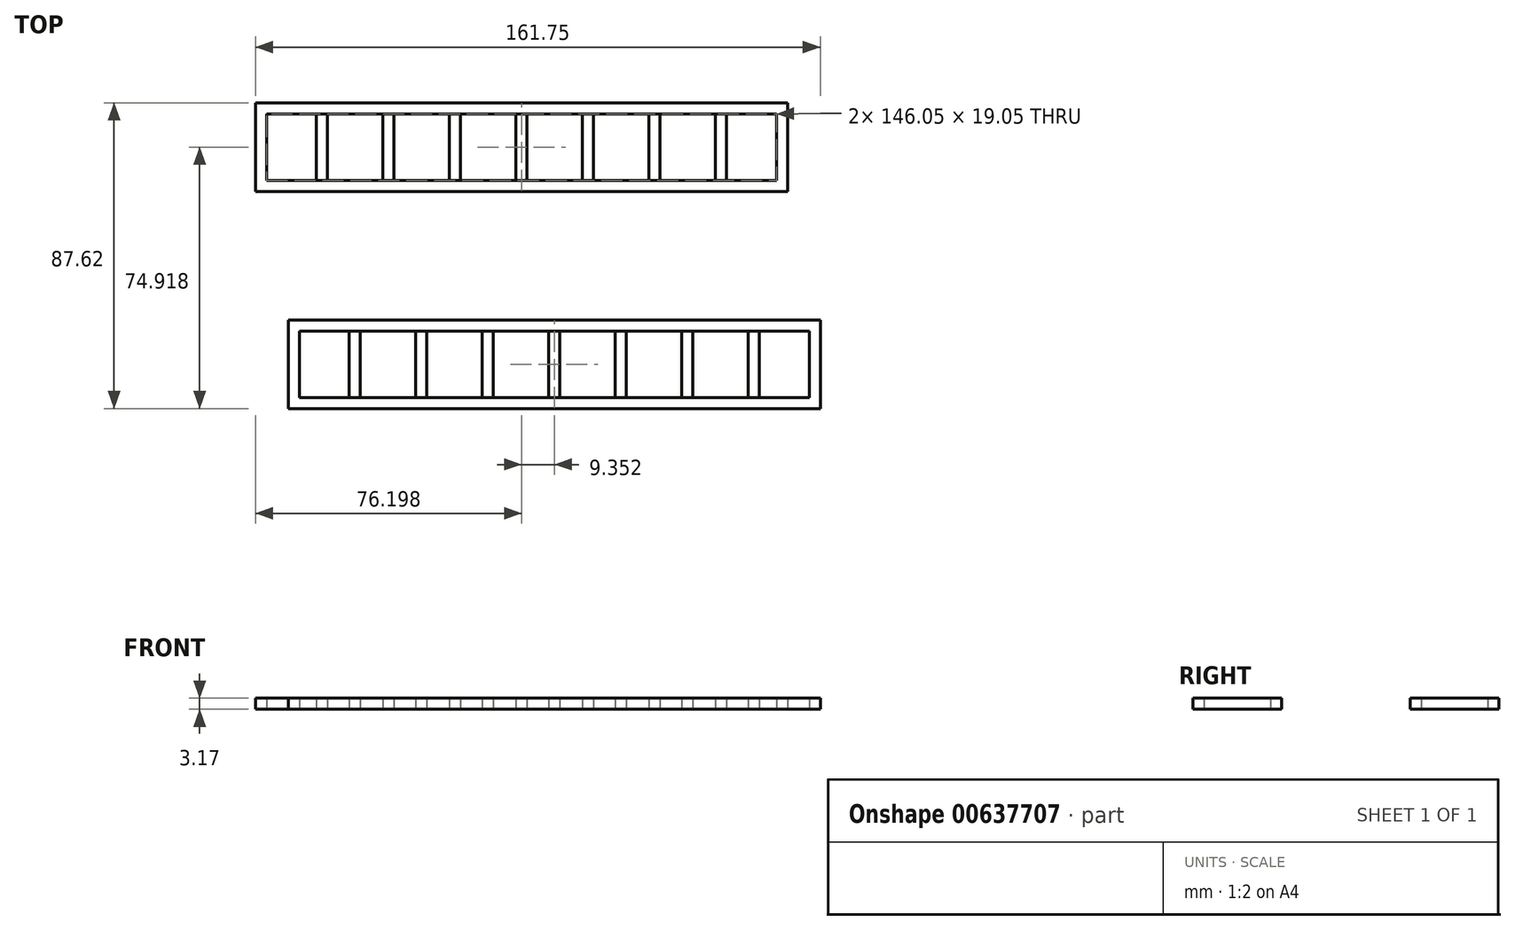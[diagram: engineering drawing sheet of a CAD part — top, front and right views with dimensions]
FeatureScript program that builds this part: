
annotation { "Feature Type Name" : "Feature", "Feature Type Description" : "" }
export const myFeature = defineFeature(function(context is Context, id is Id, definition is map)
    precondition{}
    {
        {
            var Q0;
            Q0=qCreatedBy(makeId("Top.planeOp"),FACE);
            var sketch = newSketch(context, id + "F0", { "sketchPlane" : qUnion([Q0])});
            skLineSegment(sketch, "E0.bottom", {"start": v(-74.02, 8.21) * mm, "end": v(78.38, 8.21) * mm});
            skLineSegment(sketch, "E0.top", {"start": v(-74.02, -17.19) * mm, "end": v(78.38, -17.19) * mm});
            skLineSegment(sketch, "E0.left", {"start": v(-74.02, 8.21) * mm, "end": v(-74.02, -17.19) * mm});
            skLineSegment(sketch, "E0.right", {"start": v(78.38, 8.21) * mm, "end": v(78.38, -17.19) * mm});
            skLineSegment(sketch, "E1.bottom", {"start": v(-83.37, 70.43) * mm, "end": v(69.03, 70.43) * mm});
            skLineSegment(sketch, "E1.top", {"start": v(-83.37, 45.03) * mm, "end": v(69.03, 45.03) * mm});
            skLineSegment(sketch, "E1.left", {"start": v(-83.37, 70.43) * mm, "end": v(-83.37, 45.03) * mm});
            skLineSegment(sketch, "E1.right", {"start": v(69.03, 70.43) * mm, "end": v(69.03, 45.03) * mm});
            skLineSegment(sketch, "E2", {"start": v(-80.2, 70.43) * mm, "end": v(-80.2, 45.03) * mm});
            skLineSegment(sketch, "E3", {"start": v(-83.37, 67.25) * mm, "end": v(69.03, 67.25) * mm});
            skLineSegment(sketch, "E4", {"start": v(65.85, 45.03) * mm, "end": v(65.85, 70.43) * mm});
            skLineSegment(sketch, "E5", {"start": v(69.03, 48.2) * mm, "end": v(-83.37, 48.2) * mm});
            skLineSegment(sketch, "E6", {"start": v(-70.84, 8.21) * mm, "end": v(-70.84, -17.19) * mm});
            skLineSegment(sketch, "E7", {"start": v(-74.02, 5.04) * mm, "end": v(78.38, 5.04) * mm});
            skLineSegment(sketch, "E8", {"start": v(75.2, 8.21) * mm, "end": v(75.2, -17.19) * mm});
            skLineSegment(sketch, "E9", {"start": v(-74.02, -14.01) * mm, "end": v(78.38, -14.01) * mm});
            skLineSegment(sketch, "E10", {"start": v(-54.97, 8.21) * mm, "end": v(-54.97, -17.19) * mm});
            skLineSegment(sketch, "E11", {"start": v(-35.92, 8.21) * mm, "end": v(-35.92, -17.19) * mm});
            skLineSegment(sketch, "E12", {"start": v(-16.87, 8.21) * mm, "end": v(-16.87, -17.19) * mm});
            skLineSegment(sketch, "E13", {"start": v(21.23, 8.21) * mm, "end": v(21.23, -17.19) * mm});
            skLineSegment(sketch, "E14", {"start": v(40.28, 8.21) * mm, "end": v(40.28, -17.19) * mm});
            skLineSegment(sketch, "E15", {"start": v(2.18, 8.21) * mm, "end": v(2.18, -17.19) * mm});
            skLineSegment(sketch, "E16", {"start": v(59.33, 8.21) * mm, "end": v(59.33, -17.19) * mm});
            skLineSegment(sketch, "E17", {"start": v(-64.32, 70.43) * mm, "end": v(-64.32, 45.03) * mm});
            skLineSegment(sketch, "E18", {"start": v(-45.27, 70.43) * mm, "end": v(-45.27, 45.03) * mm});
            skLineSegment(sketch, "E19", {"start": v(-26.22, 70.43) * mm, "end": v(-26.22, 45.03) * mm});
            skLineSegment(sketch, "E20", {"start": v(30.93, 70.43) * mm, "end": v(30.93, 45.03) * mm});
            skLineSegment(sketch, "E21", {"start": v(49.98, 70.43) * mm, "end": v(49.98, 45.03) * mm});
            skLineSegment(sketch, "E22", {"start": v(-7.17, 70.43) * mm, "end": v(-7.17, 45.03) * mm});
            skLineSegment(sketch, "E23", {"start": v(11.88, 70.43) * mm, "end": v(11.88, 45.03) * mm});
            skLineSegment(sketch, "E24", {"start": v(-65.9, 70.43) * mm, "end": v(-65.9, 45.03) * mm});
            skLineSegment(sketch, "E25", {"start": v(-62.73, 70.43) * mm, "end": v(-62.73, 45.03) * mm});
            skLineSegment(sketch, "E26", {"start": v(-46.86, 70.43) * mm, "end": v(-46.86, 45.03) * mm});
            skLineSegment(sketch, "E27", {"start": v(-43.68, 70.43) * mm, "end": v(-43.68, 45.03) * mm});
            skLineSegment(sketch, "E28", {"start": v(-27.8, 70.43) * mm, "end": v(-27.8, 45.03) * mm});
            skLineSegment(sketch, "E29", {"start": v(-24.63, 70.43) * mm, "end": v(-24.63, 45.03) * mm});
            skLineSegment(sketch, "E30", {"start": v(-8.76, 70.43) * mm, "end": v(-8.76, 45.03) * mm});
            skLineSegment(sketch, "E31", {"start": v(-5.58, 70.43) * mm, "end": v(-5.58, 45.03) * mm});
            skLineSegment(sketch, "E32", {"start": v(10.3, 70.43) * mm, "end": v(10.3, 45.03) * mm});
            skLineSegment(sketch, "E33", {"start": v(13.47, 70.43) * mm, "end": v(13.47, 45.03) * mm});
            skLineSegment(sketch, "E34", {"start": v(29.34, 70.43) * mm, "end": v(29.34, 45.03) * mm});
            skLineSegment(sketch, "E35", {"start": v(32.52, 70.43) * mm, "end": v(32.52, 45.03) * mm});
            skLineSegment(sketch, "E36", {"start": v(48.4, 70.43) * mm, "end": v(48.4, 45.03) * mm});
            skLineSegment(sketch, "E37", {"start": v(51.57, 70.43) * mm, "end": v(51.57, 45.03) * mm});
            skLineSegment(sketch, "E38", {"start": v(-56.56, 8.21) * mm, "end": v(-56.56, -17.19) * mm});
            skLineSegment(sketch, "E39", {"start": v(-53.38, 8.21) * mm, "end": v(-53.38, -17.19) * mm});
            skLineSegment(sketch, "E40", {"start": v(-37.5, 8.21) * mm, "end": v(-37.5, -17.19) * mm});
            skLineSegment(sketch, "E41", {"start": v(-34.33, 8.21) * mm, "end": v(-34.33, -17.19) * mm});
            skLineSegment(sketch, "E42", {"start": v(-18.46, 8.21) * mm, "end": v(-18.46, -17.19) * mm});
            skLineSegment(sketch, "E43", {"start": v(-15.28, 8.21) * mm, "end": v(-15.28, -17.19) * mm});
            skLineSegment(sketch, "E44", {"start": v(0.6, 8.21) * mm, "end": v(0.6, -17.19) * mm});
            skLineSegment(sketch, "E45", {"start": v(3.77, 8.21) * mm, "end": v(3.77, -17.19) * mm});
            skLineSegment(sketch, "E46", {"start": v(19.64, 8.21) * mm, "end": v(19.64, -17.19) * mm});
            skLineSegment(sketch, "E47", {"start": v(22.82, 8.21) * mm, "end": v(22.82, -17.19) * mm});
            skLineSegment(sketch, "E48", {"start": v(38.7, 8.21) * mm, "end": v(38.7, -17.19) * mm});
            skLineSegment(sketch, "E49", {"start": v(41.87, 8.21) * mm, "end": v(41.87, -17.19) * mm});
            skLineSegment(sketch, "E50", {"start": v(57.74, 8.21) * mm, "end": v(57.74, -17.19) * mm});
            skLineSegment(sketch, "E51", {"start": v(60.92, 8.21) * mm, "end": v(60.92, -17.19) * mm});
            skSolve(sketch);
        }
        {
            var Q0;
            {var subQ0=sQuery(id+"F0.wireOp",EDGE,"E0.left");var subQ1=sQuery(id+"F0.wireOp",EDGE,"E0.bottom");var subQ2=makeQuery(id+"F0.imprint","INTERSECT",VERTEX,{"derivedFrom":[subQ1,subQ0]});Q0=makeQuery(id+"F0.imprint","IMPRINT",FACE,{"disambiguationData":[TD([[makeQuery(id+"F0.imprint","IMPRINT",EDGE,{"disambiguationData":[TD([[subQ2,-1.0]])],"derivedFrom":subQ1}),-1.0]])]});}
            var Q1;
            {var subQ0=sQuery(id+"F0.wireOp",EDGE,"E0.right");var subQ1=sQuery(id+"F0.wireOp",EDGE,"E0.bottom");var subQ2=makeQuery(id+"F0.imprint","INTERSECT",VERTEX,{"derivedFrom":[subQ1,subQ0]});Q1=makeQuery(id+"F0.imprint","IMPRINT",FACE,{"disambiguationData":[TD([[makeQuery(id+"F0.imprint","IMPRINT",EDGE,{"disambiguationData":[TD([[subQ2,1.0]])],"derivedFrom":subQ1}),-1.0]])]});}
            var Q2;
            {var subQ0=sQuery(id+"F0.wireOp",EDGE,"E0.left");var subQ1=sQuery(id+"F0.wireOp",EDGE,"E0.top");var subQ2=makeQuery(id+"F0.imprint","INTERSECT",VERTEX,{"derivedFrom":[subQ1,subQ0]});Q2=makeQuery(id+"F0.imprint","IMPRINT",FACE,{"disambiguationData":[TD([[makeQuery(id+"F0.imprint","IMPRINT",EDGE,{"disambiguationData":[TD([[subQ2,-1.0]])],"derivedFrom":subQ1}),1.0]])]});}
            var Q3;
            {var subQ0=sQuery(id+"F0.wireOp",EDGE,"E0.right");var subQ1=sQuery(id+"F0.wireOp",EDGE,"E0.top");var subQ2=makeQuery(id+"F0.imprint","INTERSECT",VERTEX,{"derivedFrom":[subQ1,subQ0]});Q3=makeQuery(id+"F0.imprint","IMPRINT",FACE,{"disambiguationData":[TD([[makeQuery(id+"F0.imprint","IMPRINT",EDGE,{"disambiguationData":[TD([[subQ2,1.0]])],"derivedFrom":subQ1}),1.0]])]});}
            var Q4;
            {var subQ0=sQuery(id+"F0.wireOp",EDGE,"E1.right");var subQ1=sQuery(id+"F0.wireOp",EDGE,"E1.bottom");var subQ2=makeQuery(id+"F0.imprint","INTERSECT",VERTEX,{"derivedFrom":[subQ1,subQ0]});Q4=makeQuery(id+"F0.imprint","IMPRINT",FACE,{"disambiguationData":[TD([[makeQuery(id+"F0.imprint","IMPRINT",EDGE,{"disambiguationData":[TD([[subQ2,1.0]])],"derivedFrom":subQ1}),-1.0]])]});}
            var Q5;
            {var subQ0=sQuery(id+"F0.wireOp",EDGE,"E1.left");var subQ1=sQuery(id+"F0.wireOp",EDGE,"E1.top");var subQ2=makeQuery(id+"F0.imprint","INTERSECT",VERTEX,{"derivedFrom":[subQ1,subQ0]});Q5=makeQuery(id+"F0.imprint","IMPRINT",FACE,{"disambiguationData":[TD([[makeQuery(id+"F0.imprint","IMPRINT",EDGE,{"disambiguationData":[TD([[subQ2,-1.0]])],"derivedFrom":subQ1}),1.0]])]});}
            var Q6;
            {var subQ0=sQuery(id+"F0.wireOp",EDGE,"E1.right");var subQ1=sQuery(id+"F0.wireOp",EDGE,"E1.top");var subQ2=makeQuery(id+"F0.imprint","INTERSECT",VERTEX,{"derivedFrom":[subQ1,subQ0]});Q6=makeQuery(id+"F0.imprint","IMPRINT",FACE,{"disambiguationData":[TD([[makeQuery(id+"F0.imprint","IMPRINT",EDGE,{"disambiguationData":[TD([[subQ2,1.0]])],"derivedFrom":subQ1}),1.0]])]});}
            var Q7;
            {var subQ0=sQuery(id+"F0.wireOp",EDGE,"E6");var subQ1=sQuery(id+"F0.wireOp",EDGE,"E0.bottom");var subQ2=makeQuery(id+"F0.imprint","INTERSECT",VERTEX,{"derivedFrom":[subQ1,subQ0]});Q7=makeQuery(id+"F0.imprint","IMPRINT",FACE,{"disambiguationData":[TD([[makeQuery(id+"F0.imprint","IMPRINT",EDGE,{"disambiguationData":[TD([[subQ2,-1.0]])],"derivedFrom":subQ1}),-1.0]])]});}
            var Q8;
            {var subQ0=sQuery(id+"F0.wireOp",EDGE,"E10");var subQ1=sQuery(id+"F0.wireOp",EDGE,"E0.bottom");var subQ2=makeQuery(id+"F0.imprint","INTERSECT",VERTEX,{"derivedFrom":[subQ1,subQ0]});Q8=makeQuery(id+"F0.imprint","IMPRINT",FACE,{"disambiguationData":[TD([[makeQuery(id+"F0.imprint","IMPRINT",EDGE,{"disambiguationData":[TD([[subQ2,1.0]])],"derivedFrom":subQ1}),-1.0]])]});}
            var Q9;
            {var subQ0=sQuery(id+"F0.wireOp",EDGE,"E10");var subQ1=sQuery(id+"F0.wireOp",EDGE,"E0.bottom");var subQ2=makeQuery(id+"F0.imprint","INTERSECT",VERTEX,{"derivedFrom":[subQ1,subQ0]});Q9=makeQuery(id+"F0.imprint","IMPRINT",FACE,{"disambiguationData":[TD([[makeQuery(id+"F0.imprint","IMPRINT",EDGE,{"disambiguationData":[TD([[subQ2,-1.0]])],"derivedFrom":subQ1}),-1.0]])]});}
            var Q10;
            {var subQ0=sQuery(id+"F0.wireOp",EDGE,"E39");var subQ1=sQuery(id+"F0.wireOp",EDGE,"E0.bottom");var subQ2=makeQuery(id+"F0.imprint","INTERSECT",VERTEX,{"derivedFrom":[subQ1,subQ0]});Q10=makeQuery(id+"F0.imprint","IMPRINT",FACE,{"disambiguationData":[TD([[makeQuery(id+"F0.imprint","IMPRINT",EDGE,{"disambiguationData":[TD([[subQ2,-1.0]])],"derivedFrom":subQ1}),-1.0]])]});}
            var Q11;
            {var subQ0=sQuery(id+"F0.wireOp",EDGE,"E11");var subQ1=sQuery(id+"F0.wireOp",EDGE,"E0.bottom");var subQ2=makeQuery(id+"F0.imprint","INTERSECT",VERTEX,{"derivedFrom":[subQ1,subQ0]});Q11=makeQuery(id+"F0.imprint","IMPRINT",FACE,{"disambiguationData":[TD([[makeQuery(id+"F0.imprint","IMPRINT",EDGE,{"disambiguationData":[TD([[subQ2,1.0]])],"derivedFrom":subQ1}),-1.0]])]});}
            var Q12;
            {var subQ0=sQuery(id+"F0.wireOp",EDGE,"E11");var subQ1=sQuery(id+"F0.wireOp",EDGE,"E0.bottom");var subQ2=makeQuery(id+"F0.imprint","INTERSECT",VERTEX,{"derivedFrom":[subQ1,subQ0]});Q12=makeQuery(id+"F0.imprint","IMPRINT",FACE,{"disambiguationData":[TD([[makeQuery(id+"F0.imprint","IMPRINT",EDGE,{"disambiguationData":[TD([[subQ2,-1.0]])],"derivedFrom":subQ1}),-1.0]])]});}
            var Q13;
            {var subQ0=sQuery(id+"F0.wireOp",EDGE,"E41");var subQ1=sQuery(id+"F0.wireOp",EDGE,"E0.bottom");var subQ2=makeQuery(id+"F0.imprint","INTERSECT",VERTEX,{"derivedFrom":[subQ1,subQ0]});Q13=makeQuery(id+"F0.imprint","IMPRINT",FACE,{"disambiguationData":[TD([[makeQuery(id+"F0.imprint","IMPRINT",EDGE,{"disambiguationData":[TD([[subQ2,-1.0]])],"derivedFrom":subQ1}),-1.0]])]});}
            var Q14;
            {var subQ0=sQuery(id+"F0.wireOp",EDGE,"E12");var subQ1=sQuery(id+"F0.wireOp",EDGE,"E0.bottom");var subQ2=makeQuery(id+"F0.imprint","INTERSECT",VERTEX,{"derivedFrom":[subQ1,subQ0]});Q14=makeQuery(id+"F0.imprint","IMPRINT",FACE,{"disambiguationData":[TD([[makeQuery(id+"F0.imprint","IMPRINT",EDGE,{"disambiguationData":[TD([[subQ2,1.0]])],"derivedFrom":subQ1}),-1.0]])]});}
            var Q15;
            {var subQ0=sQuery(id+"F0.wireOp",EDGE,"E12");var subQ1=sQuery(id+"F0.wireOp",EDGE,"E0.bottom");var subQ2=makeQuery(id+"F0.imprint","INTERSECT",VERTEX,{"derivedFrom":[subQ1,subQ0]});Q15=makeQuery(id+"F0.imprint","IMPRINT",FACE,{"disambiguationData":[TD([[makeQuery(id+"F0.imprint","IMPRINT",EDGE,{"disambiguationData":[TD([[subQ2,-1.0]])],"derivedFrom":subQ1}),-1.0]])]});}
            var Q16;
            {var subQ0=sQuery(id+"F0.wireOp",EDGE,"E43");var subQ1=sQuery(id+"F0.wireOp",EDGE,"E0.bottom");var subQ2=makeQuery(id+"F0.imprint","INTERSECT",VERTEX,{"derivedFrom":[subQ1,subQ0]});Q16=makeQuery(id+"F0.imprint","IMPRINT",FACE,{"disambiguationData":[TD([[makeQuery(id+"F0.imprint","IMPRINT",EDGE,{"disambiguationData":[TD([[subQ2,-1.0]])],"derivedFrom":subQ1}),-1.0]])]});}
            var Q17;
            {var subQ0=sQuery(id+"F0.wireOp",EDGE,"E15");var subQ1=sQuery(id+"F0.wireOp",EDGE,"E0.bottom");var subQ2=makeQuery(id+"F0.imprint","INTERSECT",VERTEX,{"derivedFrom":[subQ1,subQ0]});Q17=makeQuery(id+"F0.imprint","IMPRINT",FACE,{"disambiguationData":[TD([[makeQuery(id+"F0.imprint","IMPRINT",EDGE,{"disambiguationData":[TD([[subQ2,1.0]])],"derivedFrom":subQ1}),-1.0]])]});}
            var Q18;
            {var subQ0=sQuery(id+"F0.wireOp",EDGE,"E15");var subQ1=sQuery(id+"F0.wireOp",EDGE,"E0.bottom");var subQ2=makeQuery(id+"F0.imprint","INTERSECT",VERTEX,{"derivedFrom":[subQ1,subQ0]});Q18=makeQuery(id+"F0.imprint","IMPRINT",FACE,{"disambiguationData":[TD([[makeQuery(id+"F0.imprint","IMPRINT",EDGE,{"disambiguationData":[TD([[subQ2,-1.0]])],"derivedFrom":subQ1}),-1.0]])]});}
            var Q19;
            {var subQ0=sQuery(id+"F0.wireOp",EDGE,"E45");var subQ1=sQuery(id+"F0.wireOp",EDGE,"E0.bottom");var subQ2=makeQuery(id+"F0.imprint","INTERSECT",VERTEX,{"derivedFrom":[subQ1,subQ0]});Q19=makeQuery(id+"F0.imprint","IMPRINT",FACE,{"disambiguationData":[TD([[makeQuery(id+"F0.imprint","IMPRINT",EDGE,{"disambiguationData":[TD([[subQ2,-1.0]])],"derivedFrom":subQ1}),-1.0]])]});}
            var Q20;
            {var subQ0=sQuery(id+"F0.wireOp",EDGE,"E13");var subQ1=sQuery(id+"F0.wireOp",EDGE,"E0.bottom");var subQ2=makeQuery(id+"F0.imprint","INTERSECT",VERTEX,{"derivedFrom":[subQ1,subQ0]});Q20=makeQuery(id+"F0.imprint","IMPRINT",FACE,{"disambiguationData":[TD([[makeQuery(id+"F0.imprint","IMPRINT",EDGE,{"disambiguationData":[TD([[subQ2,1.0]])],"derivedFrom":subQ1}),-1.0]])]});}
            var Q21;
            {var subQ0=sQuery(id+"F0.wireOp",EDGE,"E13");var subQ1=sQuery(id+"F0.wireOp",EDGE,"E0.bottom");var subQ2=makeQuery(id+"F0.imprint","INTERSECT",VERTEX,{"derivedFrom":[subQ1,subQ0]});Q21=makeQuery(id+"F0.imprint","IMPRINT",FACE,{"disambiguationData":[TD([[makeQuery(id+"F0.imprint","IMPRINT",EDGE,{"disambiguationData":[TD([[subQ2,-1.0]])],"derivedFrom":subQ1}),-1.0]])]});}
            var Q22;
            {var subQ0=sQuery(id+"F0.wireOp",EDGE,"E47");var subQ1=sQuery(id+"F0.wireOp",EDGE,"E0.bottom");var subQ2=makeQuery(id+"F0.imprint","INTERSECT",VERTEX,{"derivedFrom":[subQ1,subQ0]});Q22=makeQuery(id+"F0.imprint","IMPRINT",FACE,{"disambiguationData":[TD([[makeQuery(id+"F0.imprint","IMPRINT",EDGE,{"disambiguationData":[TD([[subQ2,-1.0]])],"derivedFrom":subQ1}),-1.0]])]});}
            var Q23;
            {var subQ0=sQuery(id+"F0.wireOp",EDGE,"E14");var subQ1=sQuery(id+"F0.wireOp",EDGE,"E0.bottom");var subQ2=makeQuery(id+"F0.imprint","INTERSECT",VERTEX,{"derivedFrom":[subQ1,subQ0]});Q23=makeQuery(id+"F0.imprint","IMPRINT",FACE,{"disambiguationData":[TD([[makeQuery(id+"F0.imprint","IMPRINT",EDGE,{"disambiguationData":[TD([[subQ2,1.0]])],"derivedFrom":subQ1}),-1.0]])]});}
            var Q24;
            {var subQ0=sQuery(id+"F0.wireOp",EDGE,"E14");var subQ1=sQuery(id+"F0.wireOp",EDGE,"E0.bottom");var subQ2=makeQuery(id+"F0.imprint","INTERSECT",VERTEX,{"derivedFrom":[subQ1,subQ0]});Q24=makeQuery(id+"F0.imprint","IMPRINT",FACE,{"disambiguationData":[TD([[makeQuery(id+"F0.imprint","IMPRINT",EDGE,{"disambiguationData":[TD([[subQ2,-1.0]])],"derivedFrom":subQ1}),-1.0]])]});}
            var Q25;
            {var subQ0=sQuery(id+"F0.wireOp",EDGE,"E49");var subQ1=sQuery(id+"F0.wireOp",EDGE,"E0.bottom");var subQ2=makeQuery(id+"F0.imprint","INTERSECT",VERTEX,{"derivedFrom":[subQ1,subQ0]});Q25=makeQuery(id+"F0.imprint","IMPRINT",FACE,{"disambiguationData":[TD([[makeQuery(id+"F0.imprint","IMPRINT",EDGE,{"disambiguationData":[TD([[subQ2,-1.0]])],"derivedFrom":subQ1}),-1.0]])]});}
            var Q26;
            {var subQ0=sQuery(id+"F0.wireOp",EDGE,"E16");var subQ1=sQuery(id+"F0.wireOp",EDGE,"E0.bottom");var subQ2=makeQuery(id+"F0.imprint","INTERSECT",VERTEX,{"derivedFrom":[subQ1,subQ0]});Q26=makeQuery(id+"F0.imprint","IMPRINT",FACE,{"disambiguationData":[TD([[makeQuery(id+"F0.imprint","IMPRINT",EDGE,{"disambiguationData":[TD([[subQ2,1.0]])],"derivedFrom":subQ1}),-1.0]])]});}
            var Q27;
            {var subQ0=sQuery(id+"F0.wireOp",EDGE,"E16");var subQ1=sQuery(id+"F0.wireOp",EDGE,"E0.bottom");var subQ2=makeQuery(id+"F0.imprint","INTERSECT",VERTEX,{"derivedFrom":[subQ1,subQ0]});Q27=makeQuery(id+"F0.imprint","IMPRINT",FACE,{"disambiguationData":[TD([[makeQuery(id+"F0.imprint","IMPRINT",EDGE,{"disambiguationData":[TD([[subQ2,-1.0]])],"derivedFrom":subQ1}),-1.0]])]});}
            var Q28;
            {var subQ0=sQuery(id+"F0.wireOp",EDGE,"E8");var subQ1=sQuery(id+"F0.wireOp",EDGE,"E0.bottom");var subQ2=makeQuery(id+"F0.imprint","INTERSECT",VERTEX,{"derivedFrom":[subQ1,subQ0]});Q28=makeQuery(id+"F0.imprint","IMPRINT",FACE,{"disambiguationData":[TD([[makeQuery(id+"F0.imprint","IMPRINT",EDGE,{"disambiguationData":[TD([[subQ2,1.0]])],"derivedFrom":subQ1}),-1.0]])]});}
            var Q29;
            {var subQ0=sQuery(id+"F0.wireOp",EDGE,"E6");var subQ1=sQuery(id+"F0.wireOp",EDGE,"E0.top");var subQ2=makeQuery(id+"F0.imprint","INTERSECT",VERTEX,{"derivedFrom":[subQ1,subQ0]});Q29=makeQuery(id+"F0.imprint","IMPRINT",FACE,{"disambiguationData":[TD([[makeQuery(id+"F0.imprint","IMPRINT",EDGE,{"disambiguationData":[TD([[subQ2,-1.0]])],"derivedFrom":subQ1}),1.0]])]});}
            var Q30;
            {var subQ0=sQuery(id+"F0.wireOp",EDGE,"E10");var subQ1=sQuery(id+"F0.wireOp",EDGE,"E0.top");var subQ2=makeQuery(id+"F0.imprint","INTERSECT",VERTEX,{"derivedFrom":[subQ1,subQ0]});Q30=makeQuery(id+"F0.imprint","IMPRINT",FACE,{"disambiguationData":[TD([[makeQuery(id+"F0.imprint","IMPRINT",EDGE,{"disambiguationData":[TD([[subQ2,1.0]])],"derivedFrom":subQ1}),1.0]])]});}
            var Q31;
            {var subQ0=sQuery(id+"F0.wireOp",EDGE,"E10");var subQ1=sQuery(id+"F0.wireOp",EDGE,"E0.top");var subQ2=makeQuery(id+"F0.imprint","INTERSECT",VERTEX,{"derivedFrom":[subQ1,subQ0]});Q31=makeQuery(id+"F0.imprint","IMPRINT",FACE,{"disambiguationData":[TD([[makeQuery(id+"F0.imprint","IMPRINT",EDGE,{"disambiguationData":[TD([[subQ2,-1.0]])],"derivedFrom":subQ1}),1.0]])]});}
            var Q32;
            {var subQ0=sQuery(id+"F0.wireOp",EDGE,"E39");var subQ1=sQuery(id+"F0.wireOp",EDGE,"E0.top");var subQ2=makeQuery(id+"F0.imprint","INTERSECT",VERTEX,{"derivedFrom":[subQ1,subQ0]});Q32=makeQuery(id+"F0.imprint","IMPRINT",FACE,{"disambiguationData":[TD([[makeQuery(id+"F0.imprint","IMPRINT",EDGE,{"disambiguationData":[TD([[subQ2,-1.0]])],"derivedFrom":subQ1}),1.0]])]});}
            var Q33;
            {var subQ0=sQuery(id+"F0.wireOp",EDGE,"E11");var subQ1=sQuery(id+"F0.wireOp",EDGE,"E0.top");var subQ2=makeQuery(id+"F0.imprint","INTERSECT",VERTEX,{"derivedFrom":[subQ1,subQ0]});Q33=makeQuery(id+"F0.imprint","IMPRINT",FACE,{"disambiguationData":[TD([[makeQuery(id+"F0.imprint","IMPRINT",EDGE,{"disambiguationData":[TD([[subQ2,1.0]])],"derivedFrom":subQ1}),1.0]])]});}
            var Q34;
            {var subQ0=sQuery(id+"F0.wireOp",EDGE,"E11");var subQ1=sQuery(id+"F0.wireOp",EDGE,"E0.top");var subQ2=makeQuery(id+"F0.imprint","INTERSECT",VERTEX,{"derivedFrom":[subQ1,subQ0]});Q34=makeQuery(id+"F0.imprint","IMPRINT",FACE,{"disambiguationData":[TD([[makeQuery(id+"F0.imprint","IMPRINT",EDGE,{"disambiguationData":[TD([[subQ2,-1.0]])],"derivedFrom":subQ1}),1.0]])]});}
            var Q35;
            {var subQ0=sQuery(id+"F0.wireOp",EDGE,"E41");var subQ1=sQuery(id+"F0.wireOp",EDGE,"E0.top");var subQ2=makeQuery(id+"F0.imprint","INTERSECT",VERTEX,{"derivedFrom":[subQ1,subQ0]});Q35=makeQuery(id+"F0.imprint","IMPRINT",FACE,{"disambiguationData":[TD([[makeQuery(id+"F0.imprint","IMPRINT",EDGE,{"disambiguationData":[TD([[subQ2,-1.0]])],"derivedFrom":subQ1}),1.0]])]});}
            var Q36;
            {var subQ0=sQuery(id+"F0.wireOp",EDGE,"E12");var subQ1=sQuery(id+"F0.wireOp",EDGE,"E0.top");var subQ2=makeQuery(id+"F0.imprint","INTERSECT",VERTEX,{"derivedFrom":[subQ1,subQ0]});Q36=makeQuery(id+"F0.imprint","IMPRINT",FACE,{"disambiguationData":[TD([[makeQuery(id+"F0.imprint","IMPRINT",EDGE,{"disambiguationData":[TD([[subQ2,1.0]])],"derivedFrom":subQ1}),1.0]])]});}
            var Q37;
            {var subQ0=sQuery(id+"F0.wireOp",EDGE,"E12");var subQ1=sQuery(id+"F0.wireOp",EDGE,"E0.top");var subQ2=makeQuery(id+"F0.imprint","INTERSECT",VERTEX,{"derivedFrom":[subQ1,subQ0]});Q37=makeQuery(id+"F0.imprint","IMPRINT",FACE,{"disambiguationData":[TD([[makeQuery(id+"F0.imprint","IMPRINT",EDGE,{"disambiguationData":[TD([[subQ2,-1.0]])],"derivedFrom":subQ1}),1.0]])]});}
            var Q38;
            {var subQ0=sQuery(id+"F0.wireOp",EDGE,"E43");var subQ1=sQuery(id+"F0.wireOp",EDGE,"E0.top");var subQ2=makeQuery(id+"F0.imprint","INTERSECT",VERTEX,{"derivedFrom":[subQ1,subQ0]});Q38=makeQuery(id+"F0.imprint","IMPRINT",FACE,{"disambiguationData":[TD([[makeQuery(id+"F0.imprint","IMPRINT",EDGE,{"disambiguationData":[TD([[subQ2,-1.0]])],"derivedFrom":subQ1}),1.0]])]});}
            var Q39;
            {var subQ0=sQuery(id+"F0.wireOp",EDGE,"E15");var subQ1=sQuery(id+"F0.wireOp",EDGE,"E0.top");var subQ2=makeQuery(id+"F0.imprint","INTERSECT",VERTEX,{"derivedFrom":[subQ1,subQ0]});Q39=makeQuery(id+"F0.imprint","IMPRINT",FACE,{"disambiguationData":[TD([[makeQuery(id+"F0.imprint","IMPRINT",EDGE,{"disambiguationData":[TD([[subQ2,1.0]])],"derivedFrom":subQ1}),1.0]])]});}
            var Q40;
            {var subQ0=sQuery(id+"F0.wireOp",EDGE,"E15");var subQ1=sQuery(id+"F0.wireOp",EDGE,"E0.top");var subQ2=makeQuery(id+"F0.imprint","INTERSECT",VERTEX,{"derivedFrom":[subQ1,subQ0]});Q40=makeQuery(id+"F0.imprint","IMPRINT",FACE,{"disambiguationData":[TD([[makeQuery(id+"F0.imprint","IMPRINT",EDGE,{"disambiguationData":[TD([[subQ2,-1.0]])],"derivedFrom":subQ1}),1.0]])]});}
            var Q41;
            {var subQ0=sQuery(id+"F0.wireOp",EDGE,"E45");var subQ1=sQuery(id+"F0.wireOp",EDGE,"E0.top");var subQ2=makeQuery(id+"F0.imprint","INTERSECT",VERTEX,{"derivedFrom":[subQ1,subQ0]});Q41=makeQuery(id+"F0.imprint","IMPRINT",FACE,{"disambiguationData":[TD([[makeQuery(id+"F0.imprint","IMPRINT",EDGE,{"disambiguationData":[TD([[subQ2,-1.0]])],"derivedFrom":subQ1}),1.0]])]});}
            var Q42;
            {var subQ0=sQuery(id+"F0.wireOp",EDGE,"E13");var subQ1=sQuery(id+"F0.wireOp",EDGE,"E0.top");var subQ2=makeQuery(id+"F0.imprint","INTERSECT",VERTEX,{"derivedFrom":[subQ1,subQ0]});Q42=makeQuery(id+"F0.imprint","IMPRINT",FACE,{"disambiguationData":[TD([[makeQuery(id+"F0.imprint","IMPRINT",EDGE,{"disambiguationData":[TD([[subQ2,1.0]])],"derivedFrom":subQ1}),1.0]])]});}
            var Q43;
            {var subQ0=sQuery(id+"F0.wireOp",EDGE,"E13");var subQ1=sQuery(id+"F0.wireOp",EDGE,"E0.top");var subQ2=makeQuery(id+"F0.imprint","INTERSECT",VERTEX,{"derivedFrom":[subQ1,subQ0]});Q43=makeQuery(id+"F0.imprint","IMPRINT",FACE,{"disambiguationData":[TD([[makeQuery(id+"F0.imprint","IMPRINT",EDGE,{"disambiguationData":[TD([[subQ2,-1.0]])],"derivedFrom":subQ1}),1.0]])]});}
            var Q44;
            {var subQ0=sQuery(id+"F0.wireOp",EDGE,"E47");var subQ1=sQuery(id+"F0.wireOp",EDGE,"E0.top");var subQ2=makeQuery(id+"F0.imprint","INTERSECT",VERTEX,{"derivedFrom":[subQ1,subQ0]});Q44=makeQuery(id+"F0.imprint","IMPRINT",FACE,{"disambiguationData":[TD([[makeQuery(id+"F0.imprint","IMPRINT",EDGE,{"disambiguationData":[TD([[subQ2,-1.0]])],"derivedFrom":subQ1}),1.0]])]});}
            var Q45;
            {var subQ0=sQuery(id+"F0.wireOp",EDGE,"E14");var subQ1=sQuery(id+"F0.wireOp",EDGE,"E0.top");var subQ2=makeQuery(id+"F0.imprint","INTERSECT",VERTEX,{"derivedFrom":[subQ1,subQ0]});Q45=makeQuery(id+"F0.imprint","IMPRINT",FACE,{"disambiguationData":[TD([[makeQuery(id+"F0.imprint","IMPRINT",EDGE,{"disambiguationData":[TD([[subQ2,1.0]])],"derivedFrom":subQ1}),1.0]])]});}
            var Q46;
            {var subQ0=sQuery(id+"F0.wireOp",EDGE,"E14");var subQ1=sQuery(id+"F0.wireOp",EDGE,"E0.top");var subQ2=makeQuery(id+"F0.imprint","INTERSECT",VERTEX,{"derivedFrom":[subQ1,subQ0]});Q46=makeQuery(id+"F0.imprint","IMPRINT",FACE,{"disambiguationData":[TD([[makeQuery(id+"F0.imprint","IMPRINT",EDGE,{"disambiguationData":[TD([[subQ2,-1.0]])],"derivedFrom":subQ1}),1.0]])]});}
            var Q47;
            {var subQ0=sQuery(id+"F0.wireOp",EDGE,"E49");var subQ1=sQuery(id+"F0.wireOp",EDGE,"E0.top");var subQ2=makeQuery(id+"F0.imprint","INTERSECT",VERTEX,{"derivedFrom":[subQ1,subQ0]});Q47=makeQuery(id+"F0.imprint","IMPRINT",FACE,{"disambiguationData":[TD([[makeQuery(id+"F0.imprint","IMPRINT",EDGE,{"disambiguationData":[TD([[subQ2,-1.0]])],"derivedFrom":subQ1}),1.0]])]});}
            var Q48;
            {var subQ0=sQuery(id+"F0.wireOp",EDGE,"E16");var subQ1=sQuery(id+"F0.wireOp",EDGE,"E0.top");var subQ2=makeQuery(id+"F0.imprint","INTERSECT",VERTEX,{"derivedFrom":[subQ1,subQ0]});Q48=makeQuery(id+"F0.imprint","IMPRINT",FACE,{"disambiguationData":[TD([[makeQuery(id+"F0.imprint","IMPRINT",EDGE,{"disambiguationData":[TD([[subQ2,1.0]])],"derivedFrom":subQ1}),1.0]])]});}
            var Q49;
            {var subQ0=sQuery(id+"F0.wireOp",EDGE,"E16");var subQ1=sQuery(id+"F0.wireOp",EDGE,"E0.top");var subQ2=makeQuery(id+"F0.imprint","INTERSECT",VERTEX,{"derivedFrom":[subQ1,subQ0]});Q49=makeQuery(id+"F0.imprint","IMPRINT",FACE,{"disambiguationData":[TD([[makeQuery(id+"F0.imprint","IMPRINT",EDGE,{"disambiguationData":[TD([[subQ2,-1.0]])],"derivedFrom":subQ1}),1.0]])]});}
            var Q50;
            {var subQ0=sQuery(id+"F0.wireOp",EDGE,"E8");var subQ1=sQuery(id+"F0.wireOp",EDGE,"E0.top");var subQ2=makeQuery(id+"F0.imprint","INTERSECT",VERTEX,{"derivedFrom":[subQ1,subQ0]});Q50=makeQuery(id+"F0.imprint","IMPRINT",FACE,{"disambiguationData":[TD([[makeQuery(id+"F0.imprint","IMPRINT",EDGE,{"disambiguationData":[TD([[subQ2,1.0]])],"derivedFrom":subQ1}),1.0]])]});}
            var Q51;
            {var subQ0=sQuery(id+"F0.wireOp",EDGE,"E7");var subQ1=sQuery(id+"F0.wireOp",EDGE,"E0.left");var subQ2=makeQuery(id+"F0.imprint","INTERSECT",VERTEX,{"derivedFrom":[subQ1,subQ0]});Q51=makeQuery(id+"F0.imprint","IMPRINT",FACE,{"disambiguationData":[TD([[makeQuery(id+"F0.imprint","IMPRINT",EDGE,{"disambiguationData":[TD([[subQ2,-1.0]])],"derivedFrom":subQ1}),1.0]])]});}
            var Q52;
            {var subQ0=sQuery(id+"F0.wireOp",EDGE,"E7");var subQ1=sQuery(id+"F0.wireOp",EDGE,"E0.right");var subQ2=makeQuery(id+"F0.imprint","INTERSECT",VERTEX,{"derivedFrom":[subQ1,subQ0]});Q52=makeQuery(id+"F0.imprint","IMPRINT",FACE,{"disambiguationData":[TD([[makeQuery(id+"F0.imprint","IMPRINT",EDGE,{"disambiguationData":[TD([[subQ2,-1.0]])],"derivedFrom":subQ1}),-1.0]])]});}
            var Q53;
            {var subQ0=sQuery(id+"F0.wireOp",EDGE,"E2");var subQ1=sQuery(id+"F0.wireOp",EDGE,"E1.bottom");var subQ2=makeQuery(id+"F0.imprint","INTERSECT",VERTEX,{"derivedFrom":[subQ1,subQ0]});Q53=makeQuery(id+"F0.imprint","IMPRINT",FACE,{"disambiguationData":[TD([[makeQuery(id+"F0.imprint","IMPRINT",EDGE,{"disambiguationData":[TD([[subQ2,-1.0]])],"derivedFrom":subQ1}),-1.0]])]});}
            var Q54;
            {var subQ0=sQuery(id+"F0.wireOp",EDGE,"E17");var subQ1=sQuery(id+"F0.wireOp",EDGE,"E1.bottom");var subQ2=makeQuery(id+"F0.imprint","INTERSECT",VERTEX,{"derivedFrom":[subQ1,subQ0]});Q54=makeQuery(id+"F0.imprint","IMPRINT",FACE,{"disambiguationData":[TD([[makeQuery(id+"F0.imprint","IMPRINT",EDGE,{"disambiguationData":[TD([[subQ2,1.0]])],"derivedFrom":subQ1}),-1.0]])]});}
            var Q55;
            {var subQ0=sQuery(id+"F0.wireOp",EDGE,"E17");var subQ1=sQuery(id+"F0.wireOp",EDGE,"E1.bottom");var subQ2=makeQuery(id+"F0.imprint","INTERSECT",VERTEX,{"derivedFrom":[subQ1,subQ0]});Q55=makeQuery(id+"F0.imprint","IMPRINT",FACE,{"disambiguationData":[TD([[makeQuery(id+"F0.imprint","IMPRINT",EDGE,{"disambiguationData":[TD([[subQ2,-1.0]])],"derivedFrom":subQ1}),-1.0]])]});}
            var Q56;
            {var subQ0=sQuery(id+"F0.wireOp",EDGE,"E25");var subQ1=sQuery(id+"F0.wireOp",EDGE,"E1.bottom");var subQ2=makeQuery(id+"F0.imprint","INTERSECT",VERTEX,{"derivedFrom":[subQ1,subQ0]});Q56=makeQuery(id+"F0.imprint","IMPRINT",FACE,{"disambiguationData":[TD([[makeQuery(id+"F0.imprint","IMPRINT",EDGE,{"disambiguationData":[TD([[subQ2,-1.0]])],"derivedFrom":subQ1}),-1.0]])]});}
            var Q57;
            {var subQ0=sQuery(id+"F0.wireOp",EDGE,"E18");var subQ1=sQuery(id+"F0.wireOp",EDGE,"E1.bottom");var subQ2=makeQuery(id+"F0.imprint","INTERSECT",VERTEX,{"derivedFrom":[subQ1,subQ0]});Q57=makeQuery(id+"F0.imprint","IMPRINT",FACE,{"disambiguationData":[TD([[makeQuery(id+"F0.imprint","IMPRINT",EDGE,{"disambiguationData":[TD([[subQ2,1.0]])],"derivedFrom":subQ1}),-1.0]])]});}
            var Q58;
            {var subQ0=sQuery(id+"F0.wireOp",EDGE,"E18");var subQ1=sQuery(id+"F0.wireOp",EDGE,"E1.bottom");var subQ2=makeQuery(id+"F0.imprint","INTERSECT",VERTEX,{"derivedFrom":[subQ1,subQ0]});Q58=makeQuery(id+"F0.imprint","IMPRINT",FACE,{"disambiguationData":[TD([[makeQuery(id+"F0.imprint","IMPRINT",EDGE,{"disambiguationData":[TD([[subQ2,-1.0]])],"derivedFrom":subQ1}),-1.0]])]});}
            var Q59;
            {var subQ0=sQuery(id+"F0.wireOp",EDGE,"E27");var subQ1=sQuery(id+"F0.wireOp",EDGE,"E1.bottom");var subQ2=makeQuery(id+"F0.imprint","INTERSECT",VERTEX,{"derivedFrom":[subQ1,subQ0]});Q59=makeQuery(id+"F0.imprint","IMPRINT",FACE,{"disambiguationData":[TD([[makeQuery(id+"F0.imprint","IMPRINT",EDGE,{"disambiguationData":[TD([[subQ2,-1.0]])],"derivedFrom":subQ1}),-1.0]])]});}
            var Q60;
            {var subQ0=sQuery(id+"F0.wireOp",EDGE,"E19");var subQ1=sQuery(id+"F0.wireOp",EDGE,"E1.bottom");var subQ2=makeQuery(id+"F0.imprint","INTERSECT",VERTEX,{"derivedFrom":[subQ1,subQ0]});Q60=makeQuery(id+"F0.imprint","IMPRINT",FACE,{"disambiguationData":[TD([[makeQuery(id+"F0.imprint","IMPRINT",EDGE,{"disambiguationData":[TD([[subQ2,1.0]])],"derivedFrom":subQ1}),-1.0]])]});}
            var Q61;
            {var subQ0=sQuery(id+"F0.wireOp",EDGE,"E19");var subQ1=sQuery(id+"F0.wireOp",EDGE,"E1.bottom");var subQ2=makeQuery(id+"F0.imprint","INTERSECT",VERTEX,{"derivedFrom":[subQ1,subQ0]});Q61=makeQuery(id+"F0.imprint","IMPRINT",FACE,{"disambiguationData":[TD([[makeQuery(id+"F0.imprint","IMPRINT",EDGE,{"disambiguationData":[TD([[subQ2,-1.0]])],"derivedFrom":subQ1}),-1.0]])]});}
            var Q62;
            {var subQ0=sQuery(id+"F0.wireOp",EDGE,"E29");var subQ1=sQuery(id+"F0.wireOp",EDGE,"E1.bottom");var subQ2=makeQuery(id+"F0.imprint","INTERSECT",VERTEX,{"derivedFrom":[subQ1,subQ0]});Q62=makeQuery(id+"F0.imprint","IMPRINT",FACE,{"disambiguationData":[TD([[makeQuery(id+"F0.imprint","IMPRINT",EDGE,{"disambiguationData":[TD([[subQ2,-1.0]])],"derivedFrom":subQ1}),-1.0]])]});}
            var Q63;
            {var subQ0=sQuery(id+"F0.wireOp",EDGE,"E22");var subQ1=sQuery(id+"F0.wireOp",EDGE,"E1.bottom");var subQ2=makeQuery(id+"F0.imprint","INTERSECT",VERTEX,{"derivedFrom":[subQ1,subQ0]});Q63=makeQuery(id+"F0.imprint","IMPRINT",FACE,{"disambiguationData":[TD([[makeQuery(id+"F0.imprint","IMPRINT",EDGE,{"disambiguationData":[TD([[subQ2,1.0]])],"derivedFrom":subQ1}),-1.0]])]});}
            var Q64;
            {var subQ0=sQuery(id+"F0.wireOp",EDGE,"E22");var subQ1=sQuery(id+"F0.wireOp",EDGE,"E1.bottom");var subQ2=makeQuery(id+"F0.imprint","INTERSECT",VERTEX,{"derivedFrom":[subQ1,subQ0]});Q64=makeQuery(id+"F0.imprint","IMPRINT",FACE,{"disambiguationData":[TD([[makeQuery(id+"F0.imprint","IMPRINT",EDGE,{"disambiguationData":[TD([[subQ2,-1.0]])],"derivedFrom":subQ1}),-1.0]])]});}
            var Q65;
            {var subQ0=sQuery(id+"F0.wireOp",EDGE,"E31");var subQ1=sQuery(id+"F0.wireOp",EDGE,"E1.bottom");var subQ2=makeQuery(id+"F0.imprint","INTERSECT",VERTEX,{"derivedFrom":[subQ1,subQ0]});Q65=makeQuery(id+"F0.imprint","IMPRINT",FACE,{"disambiguationData":[TD([[makeQuery(id+"F0.imprint","IMPRINT",EDGE,{"disambiguationData":[TD([[subQ2,-1.0]])],"derivedFrom":subQ1}),-1.0]])]});}
            var Q66;
            {var subQ0=sQuery(id+"F0.wireOp",EDGE,"E23");var subQ1=sQuery(id+"F0.wireOp",EDGE,"E1.bottom");var subQ2=makeQuery(id+"F0.imprint","INTERSECT",VERTEX,{"derivedFrom":[subQ1,subQ0]});Q66=makeQuery(id+"F0.imprint","IMPRINT",FACE,{"disambiguationData":[TD([[makeQuery(id+"F0.imprint","IMPRINT",EDGE,{"disambiguationData":[TD([[subQ2,1.0]])],"derivedFrom":subQ1}),-1.0]])]});}
            var Q67;
            {var subQ0=sQuery(id+"F0.wireOp",EDGE,"E23");var subQ1=sQuery(id+"F0.wireOp",EDGE,"E1.bottom");var subQ2=makeQuery(id+"F0.imprint","INTERSECT",VERTEX,{"derivedFrom":[subQ1,subQ0]});Q67=makeQuery(id+"F0.imprint","IMPRINT",FACE,{"disambiguationData":[TD([[makeQuery(id+"F0.imprint","IMPRINT",EDGE,{"disambiguationData":[TD([[subQ2,-1.0]])],"derivedFrom":subQ1}),-1.0]])]});}
            var Q68;
            {var subQ0=sQuery(id+"F0.wireOp",EDGE,"E33");var subQ1=sQuery(id+"F0.wireOp",EDGE,"E1.bottom");var subQ2=makeQuery(id+"F0.imprint","INTERSECT",VERTEX,{"derivedFrom":[subQ1,subQ0]});Q68=makeQuery(id+"F0.imprint","IMPRINT",FACE,{"disambiguationData":[TD([[makeQuery(id+"F0.imprint","IMPRINT",EDGE,{"disambiguationData":[TD([[subQ2,-1.0]])],"derivedFrom":subQ1}),-1.0]])]});}
            var Q69;
            {var subQ0=sQuery(id+"F0.wireOp",EDGE,"E20");var subQ1=sQuery(id+"F0.wireOp",EDGE,"E1.bottom");var subQ2=makeQuery(id+"F0.imprint","INTERSECT",VERTEX,{"derivedFrom":[subQ1,subQ0]});Q69=makeQuery(id+"F0.imprint","IMPRINT",FACE,{"disambiguationData":[TD([[makeQuery(id+"F0.imprint","IMPRINT",EDGE,{"disambiguationData":[TD([[subQ2,1.0]])],"derivedFrom":subQ1}),-1.0]])]});}
            var Q70;
            {var subQ0=sQuery(id+"F0.wireOp",EDGE,"E20");var subQ1=sQuery(id+"F0.wireOp",EDGE,"E1.bottom");var subQ2=makeQuery(id+"F0.imprint","INTERSECT",VERTEX,{"derivedFrom":[subQ1,subQ0]});Q70=makeQuery(id+"F0.imprint","IMPRINT",FACE,{"disambiguationData":[TD([[makeQuery(id+"F0.imprint","IMPRINT",EDGE,{"disambiguationData":[TD([[subQ2,-1.0]])],"derivedFrom":subQ1}),-1.0]])]});}
            var Q71;
            {var subQ0=sQuery(id+"F0.wireOp",EDGE,"E35");var subQ1=sQuery(id+"F0.wireOp",EDGE,"E1.bottom");var subQ2=makeQuery(id+"F0.imprint","INTERSECT",VERTEX,{"derivedFrom":[subQ1,subQ0]});Q71=makeQuery(id+"F0.imprint","IMPRINT",FACE,{"disambiguationData":[TD([[makeQuery(id+"F0.imprint","IMPRINT",EDGE,{"disambiguationData":[TD([[subQ2,-1.0]])],"derivedFrom":subQ1}),-1.0]])]});}
            var Q72;
            {var subQ0=sQuery(id+"F0.wireOp",EDGE,"E21");var subQ1=sQuery(id+"F0.wireOp",EDGE,"E1.bottom");var subQ2=makeQuery(id+"F0.imprint","INTERSECT",VERTEX,{"derivedFrom":[subQ1,subQ0]});Q72=makeQuery(id+"F0.imprint","IMPRINT",FACE,{"disambiguationData":[TD([[makeQuery(id+"F0.imprint","IMPRINT",EDGE,{"disambiguationData":[TD([[subQ2,1.0]])],"derivedFrom":subQ1}),-1.0]])]});}
            var Q73;
            {var subQ0=sQuery(id+"F0.wireOp",EDGE,"E21");var subQ1=sQuery(id+"F0.wireOp",EDGE,"E1.bottom");var subQ2=makeQuery(id+"F0.imprint","INTERSECT",VERTEX,{"derivedFrom":[subQ1,subQ0]});Q73=makeQuery(id+"F0.imprint","IMPRINT",FACE,{"disambiguationData":[TD([[makeQuery(id+"F0.imprint","IMPRINT",EDGE,{"disambiguationData":[TD([[subQ2,-1.0]])],"derivedFrom":subQ1}),-1.0]])]});}
            var Q74;
            {var subQ0=sQuery(id+"F0.wireOp",EDGE,"E4");var subQ1=sQuery(id+"F0.wireOp",EDGE,"E1.bottom");var subQ2=makeQuery(id+"F0.imprint","INTERSECT",VERTEX,{"derivedFrom":[subQ1,subQ0]});Q74=makeQuery(id+"F0.imprint","IMPRINT",FACE,{"disambiguationData":[TD([[makeQuery(id+"F0.imprint","IMPRINT",EDGE,{"disambiguationData":[TD([[subQ2,1.0]])],"derivedFrom":subQ1}),-1.0]])]});}
            var Q75;
            {var subQ0=sQuery(id+"F0.wireOp",EDGE,"E2");var subQ1=sQuery(id+"F0.wireOp",EDGE,"E1.top");var subQ2=makeQuery(id+"F0.imprint","INTERSECT",VERTEX,{"derivedFrom":[subQ1,subQ0]});Q75=makeQuery(id+"F0.imprint","IMPRINT",FACE,{"disambiguationData":[TD([[makeQuery(id+"F0.imprint","IMPRINT",EDGE,{"disambiguationData":[TD([[subQ2,-1.0]])],"derivedFrom":subQ1}),1.0]])]});}
            var Q76;
            {var subQ0=sQuery(id+"F0.wireOp",EDGE,"E17");var subQ1=sQuery(id+"F0.wireOp",EDGE,"E1.top");var subQ2=makeQuery(id+"F0.imprint","INTERSECT",VERTEX,{"derivedFrom":[subQ1,subQ0]});Q76=makeQuery(id+"F0.imprint","IMPRINT",FACE,{"disambiguationData":[TD([[makeQuery(id+"F0.imprint","IMPRINT",EDGE,{"disambiguationData":[TD([[subQ2,1.0]])],"derivedFrom":subQ1}),1.0]])]});}
            var Q77;
            {var subQ0=sQuery(id+"F0.wireOp",EDGE,"E17");var subQ1=sQuery(id+"F0.wireOp",EDGE,"E1.top");var subQ2=makeQuery(id+"F0.imprint","INTERSECT",VERTEX,{"derivedFrom":[subQ1,subQ0]});Q77=makeQuery(id+"F0.imprint","IMPRINT",FACE,{"disambiguationData":[TD([[makeQuery(id+"F0.imprint","IMPRINT",EDGE,{"disambiguationData":[TD([[subQ2,-1.0]])],"derivedFrom":subQ1}),1.0]])]});}
            var Q78;
            {var subQ0=sQuery(id+"F0.wireOp",EDGE,"E25");var subQ1=sQuery(id+"F0.wireOp",EDGE,"E1.top");var subQ2=makeQuery(id+"F0.imprint","INTERSECT",VERTEX,{"derivedFrom":[subQ1,subQ0]});Q78=makeQuery(id+"F0.imprint","IMPRINT",FACE,{"disambiguationData":[TD([[makeQuery(id+"F0.imprint","IMPRINT",EDGE,{"disambiguationData":[TD([[subQ2,-1.0]])],"derivedFrom":subQ1}),1.0]])]});}
            var Q79;
            {var subQ0=sQuery(id+"F0.wireOp",EDGE,"E18");var subQ1=sQuery(id+"F0.wireOp",EDGE,"E1.top");var subQ2=makeQuery(id+"F0.imprint","INTERSECT",VERTEX,{"derivedFrom":[subQ1,subQ0]});Q79=makeQuery(id+"F0.imprint","IMPRINT",FACE,{"disambiguationData":[TD([[makeQuery(id+"F0.imprint","IMPRINT",EDGE,{"disambiguationData":[TD([[subQ2,1.0]])],"derivedFrom":subQ1}),1.0]])]});}
            var Q80;
            {var subQ0=sQuery(id+"F0.wireOp",EDGE,"E18");var subQ1=sQuery(id+"F0.wireOp",EDGE,"E1.top");var subQ2=makeQuery(id+"F0.imprint","INTERSECT",VERTEX,{"derivedFrom":[subQ1,subQ0]});Q80=makeQuery(id+"F0.imprint","IMPRINT",FACE,{"disambiguationData":[TD([[makeQuery(id+"F0.imprint","IMPRINT",EDGE,{"disambiguationData":[TD([[subQ2,-1.0]])],"derivedFrom":subQ1}),1.0]])]});}
            var Q81;
            {var subQ0=sQuery(id+"F0.wireOp",EDGE,"E27");var subQ1=sQuery(id+"F0.wireOp",EDGE,"E1.top");var subQ2=makeQuery(id+"F0.imprint","INTERSECT",VERTEX,{"derivedFrom":[subQ1,subQ0]});Q81=makeQuery(id+"F0.imprint","IMPRINT",FACE,{"disambiguationData":[TD([[makeQuery(id+"F0.imprint","IMPRINT",EDGE,{"disambiguationData":[TD([[subQ2,-1.0]])],"derivedFrom":subQ1}),1.0]])]});}
            var Q82;
            {var subQ0=sQuery(id+"F0.wireOp",EDGE,"E19");var subQ1=sQuery(id+"F0.wireOp",EDGE,"E1.top");var subQ2=makeQuery(id+"F0.imprint","INTERSECT",VERTEX,{"derivedFrom":[subQ1,subQ0]});Q82=makeQuery(id+"F0.imprint","IMPRINT",FACE,{"disambiguationData":[TD([[makeQuery(id+"F0.imprint","IMPRINT",EDGE,{"disambiguationData":[TD([[subQ2,1.0]])],"derivedFrom":subQ1}),1.0]])]});}
            var Q83;
            {var subQ0=sQuery(id+"F0.wireOp",EDGE,"E19");var subQ1=sQuery(id+"F0.wireOp",EDGE,"E1.top");var subQ2=makeQuery(id+"F0.imprint","INTERSECT",VERTEX,{"derivedFrom":[subQ1,subQ0]});Q83=makeQuery(id+"F0.imprint","IMPRINT",FACE,{"disambiguationData":[TD([[makeQuery(id+"F0.imprint","IMPRINT",EDGE,{"disambiguationData":[TD([[subQ2,-1.0]])],"derivedFrom":subQ1}),1.0]])]});}
            var Q84;
            {var subQ0=sQuery(id+"F0.wireOp",EDGE,"E29");var subQ1=sQuery(id+"F0.wireOp",EDGE,"E1.top");var subQ2=makeQuery(id+"F0.imprint","INTERSECT",VERTEX,{"derivedFrom":[subQ1,subQ0]});Q84=makeQuery(id+"F0.imprint","IMPRINT",FACE,{"disambiguationData":[TD([[makeQuery(id+"F0.imprint","IMPRINT",EDGE,{"disambiguationData":[TD([[subQ2,-1.0]])],"derivedFrom":subQ1}),1.0]])]});}
            var Q85;
            {var subQ0=sQuery(id+"F0.wireOp",EDGE,"E22");var subQ1=sQuery(id+"F0.wireOp",EDGE,"E1.top");var subQ2=makeQuery(id+"F0.imprint","INTERSECT",VERTEX,{"derivedFrom":[subQ1,subQ0]});Q85=makeQuery(id+"F0.imprint","IMPRINT",FACE,{"disambiguationData":[TD([[makeQuery(id+"F0.imprint","IMPRINT",EDGE,{"disambiguationData":[TD([[subQ2,1.0]])],"derivedFrom":subQ1}),1.0]])]});}
            var Q86;
            {var subQ0=sQuery(id+"F0.wireOp",EDGE,"E22");var subQ1=sQuery(id+"F0.wireOp",EDGE,"E1.top");var subQ2=makeQuery(id+"F0.imprint","INTERSECT",VERTEX,{"derivedFrom":[subQ1,subQ0]});Q86=makeQuery(id+"F0.imprint","IMPRINT",FACE,{"disambiguationData":[TD([[makeQuery(id+"F0.imprint","IMPRINT",EDGE,{"disambiguationData":[TD([[subQ2,-1.0]])],"derivedFrom":subQ1}),1.0]])]});}
            var Q87;
            {var subQ0=sQuery(id+"F0.wireOp",EDGE,"E31");var subQ1=sQuery(id+"F0.wireOp",EDGE,"E1.top");var subQ2=makeQuery(id+"F0.imprint","INTERSECT",VERTEX,{"derivedFrom":[subQ1,subQ0]});Q87=makeQuery(id+"F0.imprint","IMPRINT",FACE,{"disambiguationData":[TD([[makeQuery(id+"F0.imprint","IMPRINT",EDGE,{"disambiguationData":[TD([[subQ2,-1.0]])],"derivedFrom":subQ1}),1.0]])]});}
            var Q88;
            {var subQ0=sQuery(id+"F0.wireOp",EDGE,"E23");var subQ1=sQuery(id+"F0.wireOp",EDGE,"E1.top");var subQ2=makeQuery(id+"F0.imprint","INTERSECT",VERTEX,{"derivedFrom":[subQ1,subQ0]});Q88=makeQuery(id+"F0.imprint","IMPRINT",FACE,{"disambiguationData":[TD([[makeQuery(id+"F0.imprint","IMPRINT",EDGE,{"disambiguationData":[TD([[subQ2,1.0]])],"derivedFrom":subQ1}),1.0]])]});}
            var Q89;
            {var subQ0=sQuery(id+"F0.wireOp",EDGE,"E23");var subQ1=sQuery(id+"F0.wireOp",EDGE,"E1.top");var subQ2=makeQuery(id+"F0.imprint","INTERSECT",VERTEX,{"derivedFrom":[subQ1,subQ0]});Q89=makeQuery(id+"F0.imprint","IMPRINT",FACE,{"disambiguationData":[TD([[makeQuery(id+"F0.imprint","IMPRINT",EDGE,{"disambiguationData":[TD([[subQ2,-1.0]])],"derivedFrom":subQ1}),1.0]])]});}
            var Q90;
            {var subQ0=sQuery(id+"F0.wireOp",EDGE,"E33");var subQ1=sQuery(id+"F0.wireOp",EDGE,"E1.top");var subQ2=makeQuery(id+"F0.imprint","INTERSECT",VERTEX,{"derivedFrom":[subQ1,subQ0]});Q90=makeQuery(id+"F0.imprint","IMPRINT",FACE,{"disambiguationData":[TD([[makeQuery(id+"F0.imprint","IMPRINT",EDGE,{"disambiguationData":[TD([[subQ2,-1.0]])],"derivedFrom":subQ1}),1.0]])]});}
            var Q91;
            {var subQ0=sQuery(id+"F0.wireOp",EDGE,"E20");var subQ1=sQuery(id+"F0.wireOp",EDGE,"E1.top");var subQ2=makeQuery(id+"F0.imprint","INTERSECT",VERTEX,{"derivedFrom":[subQ1,subQ0]});Q91=makeQuery(id+"F0.imprint","IMPRINT",FACE,{"disambiguationData":[TD([[makeQuery(id+"F0.imprint","IMPRINT",EDGE,{"disambiguationData":[TD([[subQ2,1.0]])],"derivedFrom":subQ1}),1.0]])]});}
            var Q92;
            {var subQ0=sQuery(id+"F0.wireOp",EDGE,"E20");var subQ1=sQuery(id+"F0.wireOp",EDGE,"E1.top");var subQ2=makeQuery(id+"F0.imprint","INTERSECT",VERTEX,{"derivedFrom":[subQ1,subQ0]});Q92=makeQuery(id+"F0.imprint","IMPRINT",FACE,{"disambiguationData":[TD([[makeQuery(id+"F0.imprint","IMPRINT",EDGE,{"disambiguationData":[TD([[subQ2,-1.0]])],"derivedFrom":subQ1}),1.0]])]});}
            var Q93;
            {var subQ0=sQuery(id+"F0.wireOp",EDGE,"E35");var subQ1=sQuery(id+"F0.wireOp",EDGE,"E1.top");var subQ2=makeQuery(id+"F0.imprint","INTERSECT",VERTEX,{"derivedFrom":[subQ1,subQ0]});Q93=makeQuery(id+"F0.imprint","IMPRINT",FACE,{"disambiguationData":[TD([[makeQuery(id+"F0.imprint","IMPRINT",EDGE,{"disambiguationData":[TD([[subQ2,-1.0]])],"derivedFrom":subQ1}),1.0]])]});}
            var Q94;
            {var subQ0=sQuery(id+"F0.wireOp",EDGE,"E21");var subQ1=sQuery(id+"F0.wireOp",EDGE,"E1.top");var subQ2=makeQuery(id+"F0.imprint","INTERSECT",VERTEX,{"derivedFrom":[subQ1,subQ0]});Q94=makeQuery(id+"F0.imprint","IMPRINT",FACE,{"disambiguationData":[TD([[makeQuery(id+"F0.imprint","IMPRINT",EDGE,{"disambiguationData":[TD([[subQ2,1.0]])],"derivedFrom":subQ1}),1.0]])]});}
            var Q95;
            {var subQ0=sQuery(id+"F0.wireOp",EDGE,"E21");var subQ1=sQuery(id+"F0.wireOp",EDGE,"E1.top");var subQ2=makeQuery(id+"F0.imprint","INTERSECT",VERTEX,{"derivedFrom":[subQ1,subQ0]});Q95=makeQuery(id+"F0.imprint","IMPRINT",FACE,{"disambiguationData":[TD([[makeQuery(id+"F0.imprint","IMPRINT",EDGE,{"disambiguationData":[TD([[subQ2,-1.0]])],"derivedFrom":subQ1}),1.0]])]});}
            var Q96;
            {var subQ0=sQuery(id+"F0.wireOp",EDGE,"E4");var subQ1=sQuery(id+"F0.wireOp",EDGE,"E1.top");var subQ2=makeQuery(id+"F0.imprint","INTERSECT",VERTEX,{"derivedFrom":[subQ1,subQ0]});Q96=makeQuery(id+"F0.imprint","IMPRINT",FACE,{"disambiguationData":[TD([[makeQuery(id+"F0.imprint","IMPRINT",EDGE,{"disambiguationData":[TD([[subQ2,1.0]])],"derivedFrom":subQ1}),1.0]])]});}
            var Q97;
            {var subQ0=sQuery(id+"F0.wireOp",EDGE,"E3");var subQ1=sQuery(id+"F0.wireOp",EDGE,"E1.left");var subQ2=makeQuery(id+"F0.imprint","INTERSECT",VERTEX,{"derivedFrom":[subQ1,subQ0]});Q97=makeQuery(id+"F0.imprint","IMPRINT",FACE,{"disambiguationData":[TD([[makeQuery(id+"F0.imprint","IMPRINT",EDGE,{"disambiguationData":[TD([[subQ2,-1.0]])],"derivedFrom":subQ1}),1.0]])]});}
            var Q98;
            {var subQ0=sQuery(id+"F0.wireOp",EDGE,"E3");var subQ1=sQuery(id+"F0.wireOp",EDGE,"E1.right");var subQ2=makeQuery(id+"F0.imprint","INTERSECT",VERTEX,{"derivedFrom":[subQ1,subQ0]});Q98=makeQuery(id+"F0.imprint","IMPRINT",FACE,{"disambiguationData":[TD([[makeQuery(id+"F0.imprint","IMPRINT",EDGE,{"disambiguationData":[TD([[subQ2,-1.0]])],"derivedFrom":subQ1}),-1.0]])]});}
            var Q99;
            {var subQ0=sQuery(id+"F0.wireOp",EDGE,"E1.left");var subQ1=sQuery(id+"F0.wireOp",EDGE,"E1.bottom");var subQ2=makeQuery(id+"F0.imprint","INTERSECT",VERTEX,{"derivedFrom":[subQ1,subQ0]});Q99=makeQuery(id+"F0.imprint","IMPRINT",FACE,{"disambiguationData":[TD([[makeQuery(id+"F0.imprint","IMPRINT",EDGE,{"disambiguationData":[TD([[subQ2,-1.0]])],"derivedFrom":subQ1}),-1.0]])]});}
            extrude(context, id + "F1", {"entities" : qUnion([Q0, Q1, Q2, Q3, Q4, Q5, Q6, Q7, Q8, Q9, Q10, Q11, Q12, Q13, Q14, Q15, Q16, Q17, Q18, Q19, Q20, Q21, Q22, Q23, Q24, Q25, Q26, Q27, Q28, Q29, Q30, Q31, Q32, Q33, Q34, Q35, Q36, Q37, Q38, Q39, Q40, Q41, Q42, Q43, Q44, Q45, Q46, Q47, Q48, Q49, Q50, Q51, Q52, Q53, Q54, Q55, Q56, Q57, Q58, Q59, Q60, Q61, Q62, Q63, Q64, Q65, Q66, Q67, Q68, Q69, Q70, Q71, Q72, Q73, Q74, Q75, Q76, Q77, Q78, Q79, Q80, Q81, Q82, Q83, Q84, Q85, Q86, Q87, Q88, Q89, Q90, Q91, Q92, Q93, Q94, Q95, Q96, Q97, Q98, Q99]), "depth" : 3.17 * mm, "offsetDistance" : 25.4 * mm});
        }
        {
            var Q0;
            {var subQ0=sQuery(id+"F0.wireOp",EDGE,"E24");var subQ1=sQuery(id+"F0.wireOp",EDGE,"E3");var subQ2=makeQuery(id+"F0.imprint","INTERSECT",VERTEX,{"derivedFrom":[subQ1,subQ0]});Q0=makeQuery(id+"F0.imprint","IMPRINT",FACE,{"disambiguationData":[TD([[makeQuery(id+"F0.imprint","IMPRINT",EDGE,{"disambiguationData":[TD([[subQ2,-1.0]])],"derivedFrom":subQ1}),-1.0]])]});}
            var Q1;
            {var subQ0=sQuery(id+"F0.wireOp",EDGE,"E17");var subQ1=sQuery(id+"F0.wireOp",EDGE,"E3");var subQ2=makeQuery(id+"F0.imprint","INTERSECT",VERTEX,{"derivedFrom":[subQ1,subQ0]});Q1=makeQuery(id+"F0.imprint","IMPRINT",FACE,{"disambiguationData":[TD([[makeQuery(id+"F0.imprint","IMPRINT",EDGE,{"disambiguationData":[TD([[subQ2,-1.0]])],"derivedFrom":subQ1}),-1.0]])]});}
            var Q2;
            {var subQ0=sQuery(id+"F0.wireOp",EDGE,"E26");var subQ1=sQuery(id+"F0.wireOp",EDGE,"E3");var subQ2=makeQuery(id+"F0.imprint","INTERSECT",VERTEX,{"derivedFrom":[subQ1,subQ0]});Q2=makeQuery(id+"F0.imprint","IMPRINT",FACE,{"disambiguationData":[TD([[makeQuery(id+"F0.imprint","IMPRINT",EDGE,{"disambiguationData":[TD([[subQ2,-1.0]])],"derivedFrom":subQ1}),-1.0]])]});}
            var Q3;
            {var subQ0=sQuery(id+"F0.wireOp",EDGE,"E18");var subQ1=sQuery(id+"F0.wireOp",EDGE,"E3");var subQ2=makeQuery(id+"F0.imprint","INTERSECT",VERTEX,{"derivedFrom":[subQ1,subQ0]});Q3=makeQuery(id+"F0.imprint","IMPRINT",FACE,{"disambiguationData":[TD([[makeQuery(id+"F0.imprint","IMPRINT",EDGE,{"disambiguationData":[TD([[subQ2,-1.0]])],"derivedFrom":subQ1}),-1.0]])]});}
            var Q4;
            {var subQ0=sQuery(id+"F0.wireOp",EDGE,"E28");var subQ1=sQuery(id+"F0.wireOp",EDGE,"E3");var subQ2=makeQuery(id+"F0.imprint","INTERSECT",VERTEX,{"derivedFrom":[subQ1,subQ0]});Q4=makeQuery(id+"F0.imprint","IMPRINT",FACE,{"disambiguationData":[TD([[makeQuery(id+"F0.imprint","IMPRINT",EDGE,{"disambiguationData":[TD([[subQ2,-1.0]])],"derivedFrom":subQ1}),-1.0]])]});}
            var Q5;
            {var subQ0=sQuery(id+"F0.wireOp",EDGE,"E19");var subQ1=sQuery(id+"F0.wireOp",EDGE,"E3");var subQ2=makeQuery(id+"F0.imprint","INTERSECT",VERTEX,{"derivedFrom":[subQ1,subQ0]});Q5=makeQuery(id+"F0.imprint","IMPRINT",FACE,{"disambiguationData":[TD([[makeQuery(id+"F0.imprint","IMPRINT",EDGE,{"disambiguationData":[TD([[subQ2,-1.0]])],"derivedFrom":subQ1}),-1.0]])]});}
            var Q6;
            {var subQ0=sQuery(id+"F0.wireOp",EDGE,"E30");var subQ1=sQuery(id+"F0.wireOp",EDGE,"E3");var subQ2=makeQuery(id+"F0.imprint","INTERSECT",VERTEX,{"derivedFrom":[subQ1,subQ0]});Q6=makeQuery(id+"F0.imprint","IMPRINT",FACE,{"disambiguationData":[TD([[makeQuery(id+"F0.imprint","IMPRINT",EDGE,{"disambiguationData":[TD([[subQ2,-1.0]])],"derivedFrom":subQ1}),-1.0]])]});}
            var Q7;
            {var subQ0=sQuery(id+"F0.wireOp",EDGE,"E22");var subQ1=sQuery(id+"F0.wireOp",EDGE,"E3");var subQ2=makeQuery(id+"F0.imprint","INTERSECT",VERTEX,{"derivedFrom":[subQ1,subQ0]});Q7=makeQuery(id+"F0.imprint","IMPRINT",FACE,{"disambiguationData":[TD([[makeQuery(id+"F0.imprint","IMPRINT",EDGE,{"disambiguationData":[TD([[subQ2,-1.0]])],"derivedFrom":subQ1}),-1.0]])]});}
            var Q8;
            {var subQ0=sQuery(id+"F0.wireOp",EDGE,"E32");var subQ1=sQuery(id+"F0.wireOp",EDGE,"E3");var subQ2=makeQuery(id+"F0.imprint","INTERSECT",VERTEX,{"derivedFrom":[subQ1,subQ0]});Q8=makeQuery(id+"F0.imprint","IMPRINT",FACE,{"disambiguationData":[TD([[makeQuery(id+"F0.imprint","IMPRINT",EDGE,{"disambiguationData":[TD([[subQ2,-1.0]])],"derivedFrom":subQ1}),-1.0]])]});}
            var Q9;
            {var subQ0=sQuery(id+"F0.wireOp",EDGE,"E23");var subQ1=sQuery(id+"F0.wireOp",EDGE,"E3");var subQ2=makeQuery(id+"F0.imprint","INTERSECT",VERTEX,{"derivedFrom":[subQ1,subQ0]});Q9=makeQuery(id+"F0.imprint","IMPRINT",FACE,{"disambiguationData":[TD([[makeQuery(id+"F0.imprint","IMPRINT",EDGE,{"disambiguationData":[TD([[subQ2,-1.0]])],"derivedFrom":subQ1}),-1.0]])]});}
            var Q10;
            {var subQ0=sQuery(id+"F0.wireOp",EDGE,"E34");var subQ1=sQuery(id+"F0.wireOp",EDGE,"E3");var subQ2=makeQuery(id+"F0.imprint","INTERSECT",VERTEX,{"derivedFrom":[subQ1,subQ0]});Q10=makeQuery(id+"F0.imprint","IMPRINT",FACE,{"disambiguationData":[TD([[makeQuery(id+"F0.imprint","IMPRINT",EDGE,{"disambiguationData":[TD([[subQ2,-1.0]])],"derivedFrom":subQ1}),-1.0]])]});}
            var Q11;
            {var subQ0=sQuery(id+"F0.wireOp",EDGE,"E20");var subQ1=sQuery(id+"F0.wireOp",EDGE,"E3");var subQ2=makeQuery(id+"F0.imprint","INTERSECT",VERTEX,{"derivedFrom":[subQ1,subQ0]});Q11=makeQuery(id+"F0.imprint","IMPRINT",FACE,{"disambiguationData":[TD([[makeQuery(id+"F0.imprint","IMPRINT",EDGE,{"disambiguationData":[TD([[subQ2,-1.0]])],"derivedFrom":subQ1}),-1.0]])]});}
            var Q12;
            {var subQ0=sQuery(id+"F0.wireOp",EDGE,"E36");var subQ1=sQuery(id+"F0.wireOp",EDGE,"E3");var subQ2=makeQuery(id+"F0.imprint","INTERSECT",VERTEX,{"derivedFrom":[subQ1,subQ0]});Q12=makeQuery(id+"F0.imprint","IMPRINT",FACE,{"disambiguationData":[TD([[makeQuery(id+"F0.imprint","IMPRINT",EDGE,{"disambiguationData":[TD([[subQ2,-1.0]])],"derivedFrom":subQ1}),-1.0]])]});}
            var Q13;
            {var subQ0=sQuery(id+"F0.wireOp",EDGE,"E21");var subQ1=sQuery(id+"F0.wireOp",EDGE,"E3");var subQ2=makeQuery(id+"F0.imprint","INTERSECT",VERTEX,{"derivedFrom":[subQ1,subQ0]});Q13=makeQuery(id+"F0.imprint","IMPRINT",FACE,{"disambiguationData":[TD([[makeQuery(id+"F0.imprint","IMPRINT",EDGE,{"disambiguationData":[TD([[subQ2,-1.0]])],"derivedFrom":subQ1}),-1.0]])]});}
            var Q14;
            {var subQ0=sQuery(id+"F0.wireOp",EDGE,"E38");var subQ1=sQuery(id+"F0.wireOp",EDGE,"E7");var subQ2=makeQuery(id+"F0.imprint","INTERSECT",VERTEX,{"derivedFrom":[subQ1,subQ0]});Q14=makeQuery(id+"F0.imprint","IMPRINT",FACE,{"disambiguationData":[TD([[makeQuery(id+"F0.imprint","IMPRINT",EDGE,{"disambiguationData":[TD([[subQ2,-1.0]])],"derivedFrom":subQ1}),-1.0]])]});}
            var Q15;
            {var subQ0=sQuery(id+"F0.wireOp",EDGE,"E10");var subQ1=sQuery(id+"F0.wireOp",EDGE,"E7");var subQ2=makeQuery(id+"F0.imprint","INTERSECT",VERTEX,{"derivedFrom":[subQ1,subQ0]});Q15=makeQuery(id+"F0.imprint","IMPRINT",FACE,{"disambiguationData":[TD([[makeQuery(id+"F0.imprint","IMPRINT",EDGE,{"disambiguationData":[TD([[subQ2,-1.0]])],"derivedFrom":subQ1}),-1.0]])]});}
            var Q16;
            {var subQ0=sQuery(id+"F0.wireOp",EDGE,"E40");var subQ1=sQuery(id+"F0.wireOp",EDGE,"E7");var subQ2=makeQuery(id+"F0.imprint","INTERSECT",VERTEX,{"derivedFrom":[subQ1,subQ0]});Q16=makeQuery(id+"F0.imprint","IMPRINT",FACE,{"disambiguationData":[TD([[makeQuery(id+"F0.imprint","IMPRINT",EDGE,{"disambiguationData":[TD([[subQ2,-1.0]])],"derivedFrom":subQ1}),-1.0]])]});}
            var Q17;
            {var subQ0=sQuery(id+"F0.wireOp",EDGE,"E11");var subQ1=sQuery(id+"F0.wireOp",EDGE,"E7");var subQ2=makeQuery(id+"F0.imprint","INTERSECT",VERTEX,{"derivedFrom":[subQ1,subQ0]});Q17=makeQuery(id+"F0.imprint","IMPRINT",FACE,{"disambiguationData":[TD([[makeQuery(id+"F0.imprint","IMPRINT",EDGE,{"disambiguationData":[TD([[subQ2,-1.0]])],"derivedFrom":subQ1}),-1.0]])]});}
            var Q18;
            {var subQ0=sQuery(id+"F0.wireOp",EDGE,"E42");var subQ1=sQuery(id+"F0.wireOp",EDGE,"E7");var subQ2=makeQuery(id+"F0.imprint","INTERSECT",VERTEX,{"derivedFrom":[subQ1,subQ0]});Q18=makeQuery(id+"F0.imprint","IMPRINT",FACE,{"disambiguationData":[TD([[makeQuery(id+"F0.imprint","IMPRINT",EDGE,{"disambiguationData":[TD([[subQ2,-1.0]])],"derivedFrom":subQ1}),-1.0]])]});}
            var Q19;
            {var subQ0=sQuery(id+"F0.wireOp",EDGE,"E12");var subQ1=sQuery(id+"F0.wireOp",EDGE,"E7");var subQ2=makeQuery(id+"F0.imprint","INTERSECT",VERTEX,{"derivedFrom":[subQ1,subQ0]});Q19=makeQuery(id+"F0.imprint","IMPRINT",FACE,{"disambiguationData":[TD([[makeQuery(id+"F0.imprint","IMPRINT",EDGE,{"disambiguationData":[TD([[subQ2,-1.0]])],"derivedFrom":subQ1}),-1.0]])]});}
            var Q20;
            {var subQ0=sQuery(id+"F0.wireOp",EDGE,"E44");var subQ1=sQuery(id+"F0.wireOp",EDGE,"E7");var subQ2=makeQuery(id+"F0.imprint","INTERSECT",VERTEX,{"derivedFrom":[subQ1,subQ0]});Q20=makeQuery(id+"F0.imprint","IMPRINT",FACE,{"disambiguationData":[TD([[makeQuery(id+"F0.imprint","IMPRINT",EDGE,{"disambiguationData":[TD([[subQ2,-1.0]])],"derivedFrom":subQ1}),-1.0]])]});}
            var Q21;
            {var subQ0=sQuery(id+"F0.wireOp",EDGE,"E15");var subQ1=sQuery(id+"F0.wireOp",EDGE,"E7");var subQ2=makeQuery(id+"F0.imprint","INTERSECT",VERTEX,{"derivedFrom":[subQ1,subQ0]});Q21=makeQuery(id+"F0.imprint","IMPRINT",FACE,{"disambiguationData":[TD([[makeQuery(id+"F0.imprint","IMPRINT",EDGE,{"disambiguationData":[TD([[subQ2,-1.0]])],"derivedFrom":subQ1}),-1.0]])]});}
            var Q22;
            {var subQ0=sQuery(id+"F0.wireOp",EDGE,"E46");var subQ1=sQuery(id+"F0.wireOp",EDGE,"E7");var subQ2=makeQuery(id+"F0.imprint","INTERSECT",VERTEX,{"derivedFrom":[subQ1,subQ0]});Q22=makeQuery(id+"F0.imprint","IMPRINT",FACE,{"disambiguationData":[TD([[makeQuery(id+"F0.imprint","IMPRINT",EDGE,{"disambiguationData":[TD([[subQ2,-1.0]])],"derivedFrom":subQ1}),-1.0]])]});}
            var Q23;
            {var subQ0=sQuery(id+"F0.wireOp",EDGE,"E13");var subQ1=sQuery(id+"F0.wireOp",EDGE,"E7");var subQ2=makeQuery(id+"F0.imprint","INTERSECT",VERTEX,{"derivedFrom":[subQ1,subQ0]});Q23=makeQuery(id+"F0.imprint","IMPRINT",FACE,{"disambiguationData":[TD([[makeQuery(id+"F0.imprint","IMPRINT",EDGE,{"disambiguationData":[TD([[subQ2,-1.0]])],"derivedFrom":subQ1}),-1.0]])]});}
            var Q24;
            {var subQ0=sQuery(id+"F0.wireOp",EDGE,"E48");var subQ1=sQuery(id+"F0.wireOp",EDGE,"E7");var subQ2=makeQuery(id+"F0.imprint","INTERSECT",VERTEX,{"derivedFrom":[subQ1,subQ0]});Q24=makeQuery(id+"F0.imprint","IMPRINT",FACE,{"disambiguationData":[TD([[makeQuery(id+"F0.imprint","IMPRINT",EDGE,{"disambiguationData":[TD([[subQ2,-1.0]])],"derivedFrom":subQ1}),-1.0]])]});}
            var Q25;
            {var subQ0=sQuery(id+"F0.wireOp",EDGE,"E14");var subQ1=sQuery(id+"F0.wireOp",EDGE,"E7");var subQ2=makeQuery(id+"F0.imprint","INTERSECT",VERTEX,{"derivedFrom":[subQ1,subQ0]});Q25=makeQuery(id+"F0.imprint","IMPRINT",FACE,{"disambiguationData":[TD([[makeQuery(id+"F0.imprint","IMPRINT",EDGE,{"disambiguationData":[TD([[subQ2,-1.0]])],"derivedFrom":subQ1}),-1.0]])]});}
            var Q26;
            {var subQ0=sQuery(id+"F0.wireOp",EDGE,"E50");var subQ1=sQuery(id+"F0.wireOp",EDGE,"E7");var subQ2=makeQuery(id+"F0.imprint","INTERSECT",VERTEX,{"derivedFrom":[subQ1,subQ0]});Q26=makeQuery(id+"F0.imprint","IMPRINT",FACE,{"disambiguationData":[TD([[makeQuery(id+"F0.imprint","IMPRINT",EDGE,{"disambiguationData":[TD([[subQ2,-1.0]])],"derivedFrom":subQ1}),-1.0]])]});}
            var Q27;
            {var subQ0=sQuery(id+"F0.wireOp",EDGE,"E16");var subQ1=sQuery(id+"F0.wireOp",EDGE,"E7");var subQ2=makeQuery(id+"F0.imprint","INTERSECT",VERTEX,{"derivedFrom":[subQ1,subQ0]});Q27=makeQuery(id+"F0.imprint","IMPRINT",FACE,{"disambiguationData":[TD([[makeQuery(id+"F0.imprint","IMPRINT",EDGE,{"disambiguationData":[TD([[subQ2,-1.0]])],"derivedFrom":subQ1}),-1.0]])]});}
            extrude(context, id + "F2", {"entities" : qUnion([Q0, Q1, Q2, Q3, Q4, Q5, Q6, Q7, Q8, Q9, Q10, Q11, Q12, Q13, Q14, Q15, Q16, Q17, Q18, Q19, Q20, Q21, Q22, Q23, Q24, Q25, Q26, Q27]), "depth" : 3.17 * mm, "offsetDistance" : 25.4 * mm});
        }
    });
